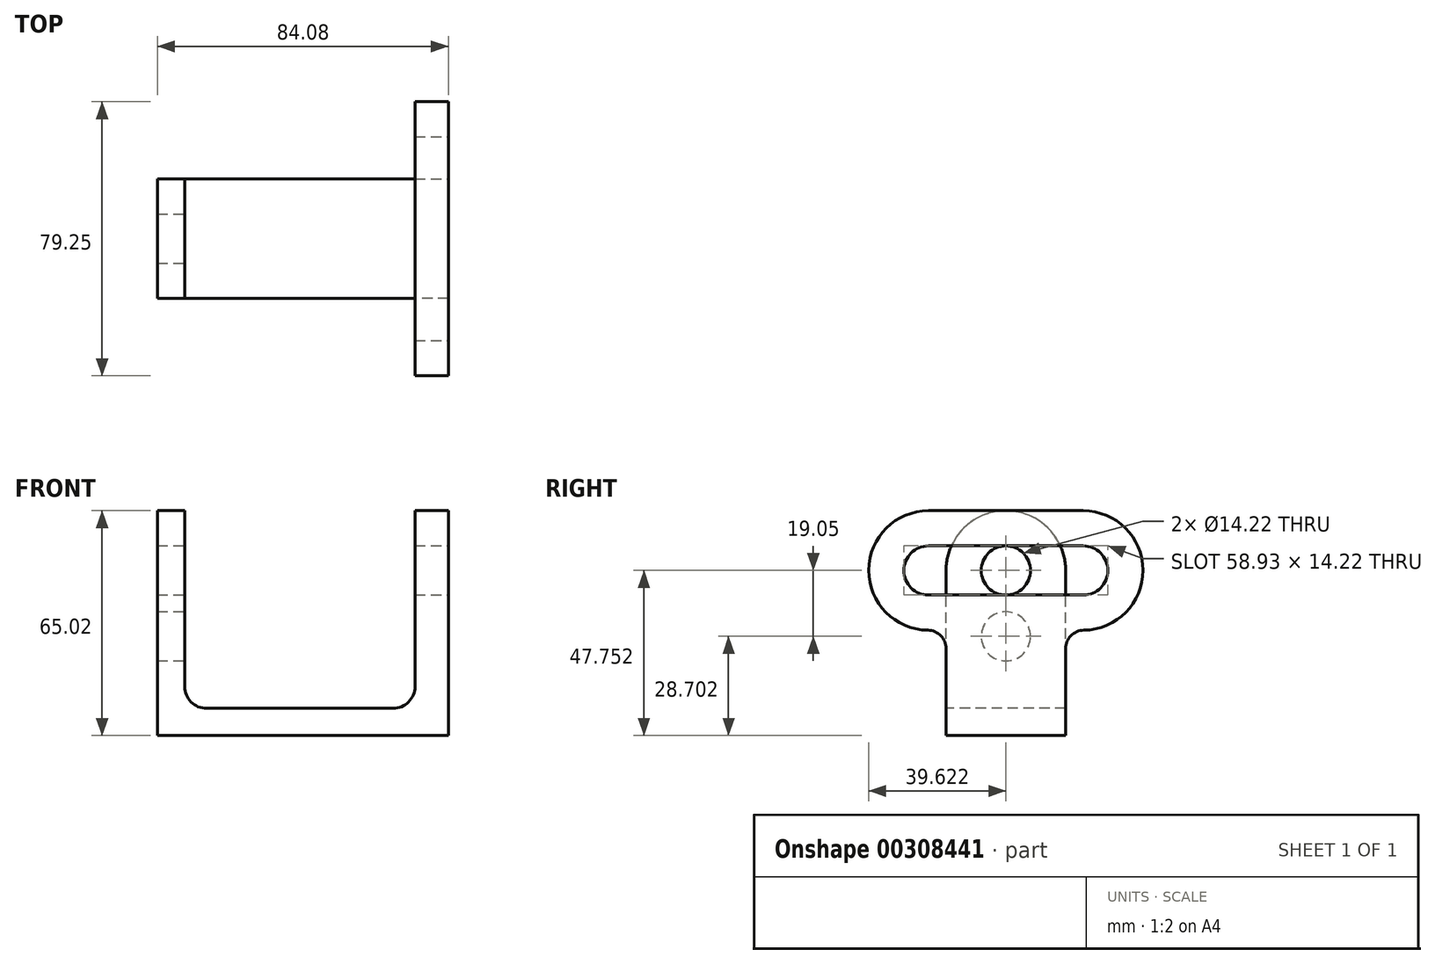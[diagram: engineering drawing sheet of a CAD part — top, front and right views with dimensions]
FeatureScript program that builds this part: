
annotation { "Feature Type Name" : "Feature", "Feature Type Description" : "" }
export const myFeature = defineFeature(function(context is Context, id is Id, definition is map)
    precondition{}
    {
        {
            var Q0;
            Q0=qCreatedBy(makeId("Front.planeOp"),FACE);
            var sketch = newSketch(context, id + "F0", { "sketchPlane" : qUnion([Q0])});
            skLineSegment(sketch, "E0.bottom", {"start": v(-42.04, 0) * mm, "end": v(42.04, 0) * mm});
            skLineSegment(sketch, "E0.top", {"start": v(-42.04, 47.75) * mm, "end": v(42.04, 47.75) * mm});
            skLineSegment(sketch, "E0.left", {"start": v(-42.04, 0) * mm, "end": v(-42.04, 47.75) * mm});
            skLineSegment(sketch, "E0.right", {"start": v(42.04, 0) * mm, "end": v(42.04, 47.75) * mm});
            skSolve(sketch);
        }
        {
            var Q0;
            Q0 = qSketchRegion(id + "F0", true);
            extrude(context, id + "F1", {"entities" : qUnion([Q0]), "oppositeDirection" : true, "depth" : 34.54 * mm});
        }
        {
            var Q0;
            Q0=qCreatedBy(makeId("Front.planeOp"),FACE);
            var sketch = newSketch(context, id + "F2", { "sketchPlane" : qUnion([Q0])});
            skLineSegment(sketch, "E1", {"start": v(-42.04, 7.87) * mm, "end": v(-34.16, 7.87) * mm});
            skLineSegment(sketch, "E2", {"start": v(-34.16, 7.87) * mm, "end": v(-34.16, 0) * mm});
            skLineSegment(sketch, "E3", {"start": v(42.04, 0) * mm, "end": v(32.39, 0) * mm});
            skLineSegment(sketch, "E4", {"start": v(32.39, 0) * mm, "end": v(32.39, 7.87) * mm});
            skLineSegment(sketch, "E5", {"start": v(32.39, 7.87) * mm, "end": v(42.04, 7.87) * mm});
            skLineSegment(sketch, "E6", {"start": v(42.04, 7.87) * mm, "end": v(42.04, 0) * mm});
            skLineSegment(sketch, "E7", {"start": v(-42.04, 7.87) * mm, "end": v(-42.04, 0) * mm});
            skLineSegment(sketch, "E8", {"start": v(-42.04, 0) * mm, "end": v(-34.16, 0) * mm});
            skLineSegment(sketch, "E9", {"start": v(-34.16, 7.87) * mm, "end": v(32.39, 7.87) * mm});
            skLineSegment(sketch, "E10", {"start": v(-34.16, 7.87) * mm, "end": v(-34.16, 47.75) * mm});
            skLineSegment(sketch, "E11", {"start": v(-34.16, 47.75) * mm, "end": v(32.39, 47.75) * mm});
            skLineSegment(sketch, "E12", {"start": v(32.39, 47.75) * mm, "end": v(32.39, 7.87) * mm});
            skSolve(sketch);
        }
        {
            var Q0;
            Q0=makeQuery(id+"F2.imprint","IMPRINT",FACE,{"disambiguationData":[TD([[makeQuery(id+"F2.imprint","IMPRINT",EDGE,{"derivedFrom":sQuery(id+"F2.wireOp",EDGE,"E9")}),1.0]])]});
            extrude(context, id + "F3", {"entities" : qUnion([Q0]), "operationType" : NewBodyOperationType.REMOVE, "endBound" : BoundingType.THROUGH_ALL, "oppositeDirection" : true, "depth" : 25.4 * mm});
        }
        {
            var Q0;
            Q0=makeQuery(id+"F3.boolean.opBoolean","COPY",EDGE,{"derivedFrom":makeQuery(id+"F3.opExtrude","SWEPT_EDGE",EDGE,{"disambiguationData":[OSD([sQuery(id+"F2.wireOp",EDGE,"E1"),sQuery(id+"F2.wireOp",EDGE,"E2"),sQuery(id+"F2.wireOp",EDGE,"E9"),sQuery(id+"F2.wireOp",EDGE,"E10")])]})});
            var Q1;
            Q1=makeQuery(id+"F3.boolean.opBoolean","COPY",EDGE,{"derivedFrom":makeQuery(id+"F3.opExtrude","SWEPT_EDGE",EDGE,{"disambiguationData":[OSD([sQuery(id+"F2.wireOp",EDGE,"E4"),sQuery(id+"F2.wireOp",EDGE,"E5"),sQuery(id+"F2.wireOp",EDGE,"E9"),sQuery(id+"F2.wireOp",EDGE,"E12")])]})});
            fillet(context, id + "F4", {"entities" : qUnion([Q0, Q1]), "radius" : 6.35 * mm, "tangentPropagation" : true, "allowEdgeOverflow" : false});
        }
        {
            var Q0;
            Q0=makeQuery(id+"F3.boolean.opBoolean","COPY",FACE,{"derivedFrom":makeQuery(id+"F3.opExtrude","SWEPT_FACE",FACE,{"disambiguationData":[OSD([sQuery(id+"F2.wireOp",EDGE,"E10")])]})});
            var sketch = newSketch(context, id + "F5", { "sketchPlane" : qUnion([Q0])});
            skArc(sketch, "E13", {"start": v(34.54, 47.75) * mm, "mid": v(17.27, 65.02) * mm, "end": v(0, 47.75) * mm});
            skLineSegment(sketch, "E14", {"start": v(0, 47.75) * mm, "end": v(34.54, 47.75) * mm});
            skSolve(sketch);
        }
        {
            var Q0;
            Q0 = qSketchRegion(id + "F5", true);
            extrude(context, id + "F6", {"entities" : qUnion([Q0]), "operationType" : NewBodyOperationType.ADD, "oppositeDirection" : true, "depth" : 7.87 * mm});
        }
        {
            var Q0;
            Q0=makeQuery(id+"F6.boolean.opBoolean","MERGE",FACE,{"derivedFrom":[makeQuery(id+"F3.boolean.opBoolean","COPY",FACE,{"derivedFrom":makeQuery(id+"F3.opExtrude","SWEPT_FACE",FACE,{"disambiguationData":[OSD([sQuery(id+"F2.wireOp",EDGE,"E10")])]})}),makeQuery(id+"F6.opExtrude","CAP_FACE",FACE,{"disambiguationData":[OSD([sQuery(id+"F5.wireOp",EDGE,"E13"),sQuery(id+"F5.wireOp",EDGE,"E14")])],"isStart":true})]});
            var sketch = newSketch(context, id + "F7", { "sketchPlane" : qUnion([Q0])});
            skCircle(sketch, "E15", {"center": v(17.27, 47.75) * mm, "radius": 7.11 * mm});
            skCircle(sketch, "E16", {"center": v(17.27, 28.7) * mm, "radius": 7.11 * mm});
            skSolve(sketch);
        }
        {
            var Q0;
            Q0 = qSketchRegion(id + "F7", true);
            extrude(context, id + "F8", {"entities" : qUnion([Q0]), "operationType" : NewBodyOperationType.REMOVE, "oppositeDirection" : true, "depth" : 25.4 * mm});
        }
        {
            var Q0;
            Q0=makeQuery(id+"F1.opExtrude","SWEPT_FACE",FACE,{"disambiguationData":[OSD([sQuery(id+"F0.wireOp",EDGE,"E0.right")])]});
            var sketch = newSketch(context, id + "F9", { "sketchPlane" : qUnion([Q0])});
            skLineSegment(sketch, "E17", {"start": v(17.27, 47.75) * mm, "end": v(-5.08, 47.75) * mm});
            skLineSegment(sketch, "E18", {"start": v(17.27, 47.75) * mm, "end": v(39.62, 47.75) * mm});
            skArc(sketch, "E19", {"start": v(-5.08, 30.48) * mm, "mid": v(-22.35, 47.75) * mm, "end": v(-5.08, 65.02) * mm});
            skArc(sketch, "E20", {"start": v(39.62, 65.02) * mm, "mid": v(56.9, 47.75) * mm, "end": v(39.62, 30.48) * mm});
            skLineSegment(sketch, "E21", {"start": v(-5.08, 65.02) * mm, "end": v(39.62, 65.02) * mm});
            skLineSegment(sketch, "E22", {"start": v(-5.08, 30.48) * mm, "end": v(39.62, 30.48) * mm});
            skArc(sketch, "E23", {"start": v(-5.08, 54.86) * mm, "mid": v(-12.2, 47.75) * mm, "end": v(-5.08, 40.64) * mm});
            skArc(sketch, "E24", {"start": v(39.62, 54.86) * mm, "mid": v(46.74, 47.75) * mm, "end": v(39.62, 40.64) * mm});
            skLineSegment(sketch, "E25", {"start": v(-5.08, 54.86) * mm, "end": v(39.62, 54.86) * mm});
            skLineSegment(sketch, "E26", {"start": v(-5.08, 40.64) * mm, "end": v(39.62, 40.64) * mm});
            skSolve(sketch);
        }
        {
            var Q0;
            Q0 = qSketchRegion(id + "F9", true);
            extrude(context, id + "F10", {"entities" : qUnion([Q0]), "operationType" : NewBodyOperationType.ADD, "oppositeDirection" : true, "depth" : 9.65 * mm});
        }
        {
            var Q0;
            Q0=makeQuery(id+"F10.boolean.opBoolean","MERGE",FACE,{"derivedFrom":[makeQuery(id+"F1.opExtrude","SWEPT_FACE",FACE,{"disambiguationData":[OSD([sQuery(id+"F0.wireOp",EDGE,"E0.right")])]}),makeQuery(id+"F10.opExtrude","CAP_FACE",FACE,{"disambiguationData":[OSD([sQuery(id+"F9.wireOp",EDGE,"E19"),sQuery(id+"F9.wireOp",EDGE,"E20"),sQuery(id+"F9.wireOp",EDGE,"E21"),sQuery(id+"F9.wireOp",EDGE,"E22"),sQuery(id+"F9.wireOp",EDGE,"E23"),sQuery(id+"F9.wireOp",EDGE,"E24"),sQuery(id+"F9.wireOp",EDGE,"E25"),sQuery(id+"F9.wireOp",EDGE,"E26")])],"isStart":true})]});
            var sketch = newSketch(context, id + "F11", { "sketchPlane" : qUnion([Q0])});
            skLineSegment(sketch, "E27.bottom", {"start": v(0, 47.75) * mm, "end": v(34.54, 47.75) * mm});
            skLineSegment(sketch, "E27.top", {"start": v(0, 40.64) * mm, "end": v(34.54, 40.64) * mm});
            skLineSegment(sketch, "E27.left", {"start": v(0, 47.75) * mm, "end": v(0, 40.64) * mm});
            skLineSegment(sketch, "E27.right", {"start": v(34.54, 47.75) * mm, "end": v(34.54, 40.64) * mm});
            skSolve(sketch);
        }
        {
            var Q0;
            Q0 = qSketchRegion(id + "F11", true);
            extrude(context, id + "F12", {"entities" : qUnion([Q0]), "operationType" : NewBodyOperationType.REMOVE, "oppositeDirection" : true, "depth" : 25.4 * mm});
        }
        {
            var Q0;
            Q0=makeQuery(id+"F10.boolean.opBoolean","INTERSECT",EDGE,{"derivedFrom":[makeQuery(id+"F1.opExtrude","CAP_FACE",FACE,{"disambiguationData":[OSD([sQuery(id+"F0.wireOp",EDGE,"E0.bottom"),sQuery(id+"F0.wireOp",EDGE,"E0.top"),sQuery(id+"F0.wireOp",EDGE,"E0.left"),sQuery(id+"F0.wireOp",EDGE,"E0.right")])],"isStart":true}),makeQuery(id+"F10.opExtrude","SWEPT_FACE",FACE,{"disambiguationData":[OSD([sQuery(id+"F9.wireOp",EDGE,"E22")])]})]});
            var Q1;
            Q1=makeQuery(id+"F10.boolean.opBoolean","INTERSECT",EDGE,{"derivedFrom":[makeQuery(id+"F1.opExtrude","CAP_FACE",FACE,{"disambiguationData":[OSD([sQuery(id+"F0.wireOp",EDGE,"E0.bottom"),sQuery(id+"F0.wireOp",EDGE,"E0.top"),sQuery(id+"F0.wireOp",EDGE,"E0.left"),sQuery(id+"F0.wireOp",EDGE,"E0.right")])],"isStart":false}),makeQuery(id+"F10.opExtrude","SWEPT_FACE",FACE,{"disambiguationData":[OSD([sQuery(id+"F9.wireOp",EDGE,"E22")])]})]});
            fillet(context, id + "F13", {"entities" : qUnion([Q0, Q1]), "radius" : 5.33 * mm, "tangentPropagation" : true, "allowEdgeOverflow" : false});
        }
    });
